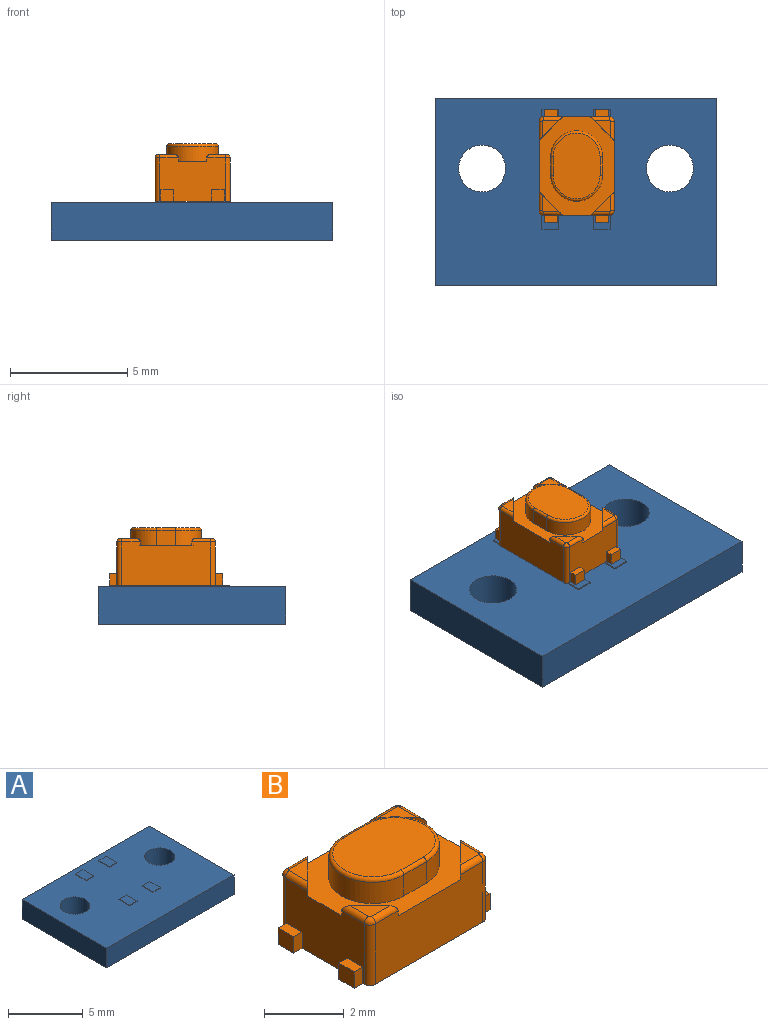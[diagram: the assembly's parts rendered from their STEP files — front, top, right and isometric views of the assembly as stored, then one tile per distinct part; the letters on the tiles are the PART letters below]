
ASSEMBLY  parts=2 mates=1
PART A: 28 faces, bbox 12x8x1.7 mm
  f0: plane 12x8mm, normal (0,0,1), area 86.9mm2, adj f1,f2,f3,f4,f5,f6,f8,f9
  f1: plane 12x1.6mm, normal (0,1,0), area 19.2mm2, adj f0,f2,f6,f7
  f2: plane 8x1.6mm, normal (-1,0,0), area 12.8mm2, adj f0,f1,f3,f7
  f3: plane 12x1.6mm, normal (0,-1,0), area 19.2mm2, adj f0,f2,f6,f7
  f4: cylinder r=1mm len=2mm, axis (0,0,-1), area 10.1mm2, adj f0,f7
  f5: cylinder r=1mm len=2mm, axis (0,0,-1), area 10.1mm2, adj f0,f7
  f6: plane 8x1.6mm, normal (1,0,0), area 12.8mm2, adj f0,f1,f3,f7
  f7: plane 12x8mm, normal (0,0,-1), area 89.7mm2, adj f1,f2,f3,f4,f5,f6
  f8: plane 1x0.05mm, normal (-1,0,0), area 0mm2, adj f0,f9,f11,f12
  f9: plane 0.7x0.05mm, normal (0,-1,0), area 0mm2, adj f0,f8,f10,f12
  f10: plane 1x0.05mm, normal (1,0,0), area 0mm2, adj f0,f9,f11,f12
  f11: plane 0.7x0.05mm, normal (0,1,0), area 0mm2, adj f0,f8,f10,f12
  f12: plane 1x0.7mm, normal (0,0,1), area 0.7mm2, adj f8,f9,f10,f11
  f13: plane 1x0.05mm, normal (-1,0,0), area 0mm2, adj f0,f14,f16,f17
  f14: plane 0.7x0.05mm, normal (0,-1,0), area 0mm2, adj f0,f13,f15,f17
  f15: plane 1x0.05mm, normal (1,0,0), area 0mm2, adj f0,f14,f16,f17
  f16: plane 0.7x0.05mm, normal (0,1,0), area 0mm2, adj f0,f13,f15,f17
  f17: plane 1x0.7mm, normal (0,0,1), area 0.7mm2, adj f13,f14,f15,f16
  f18: plane 1x0.05mm, normal (-1,0,0), area 0mm2, adj f0,f19,f21,f22
  f19: plane 0.7x0.05mm, normal (0,-1,0), area 0mm2, adj f0,f18,f20,f22
  f20: plane 1x0.05mm, normal (1,0,0), area 0mm2, adj f0,f19,f21,f22
  f21: plane 0.7x0.05mm, normal (0,1,0), area 0mm2, adj f0,f18,f20,f22
  f22: plane 1x0.7mm, normal (0,0,1), area 0.7mm2, adj f18,f19,f20,f21
  f23: plane 1x0.05mm, normal (-1,0,0), area 0mm2, adj f0,f24,f26,f27
  f24: plane 0.7x0.05mm, normal (0,-1,0), area 0mm2, adj f0,f23,f25,f27
  f25: plane 1x0.05mm, normal (1,0,0), area 0mm2, adj f0,f24,f26,f27
  f26: plane 0.7x0.05mm, normal (0,1,0), area 0mm2, adj f0,f23,f25,f27
  f27: plane 1x0.7mm, normal (0,0,1), area 0.7mm2, adj f23,f24,f25,f26
PART B: 55 faces, bbox 4.8x3.2x2.5 mm
  f0: plane 4.2x3.2mm, normal (0,0,1), area 5.9mm2, adj f1,f2,f3,f4,f26,f27,f28,f29
  f1: plane 3.8x1.85mm, normal (0,1,0), area 6.7mm2, adj f0,f5,f6,f9,f33,f35,f39,f50
  f2: plane 2.8x1.85mm, normal (-1,0,0), area 4.4mm2, adj f0,f5,f6,f7,f14,f15,f16,f22
  f3: plane 3.8x1.85mm, normal (0,-1,0), area 6.7mm2, adj f0,f5,f7,f8,f31,f37,f42,f47
  f4: plane 2.8x1.85mm, normal (1,0,0), area 4.4mm2, adj f0,f5,f8,f9,f11,f12,f13,f19
  f5: plane 4.8x3.2mm, normal (0,0,-1), area 14.1mm2, adj f1,f2,f3,f4,f6,f7,f8,f9
  f6: cylinder r=0.2mm len=1.85mm, axis (0,0,1), area 0.6mm2, adj f1,f2,f5,f49
  f7: cylinder r=0.2mm len=1.85mm, axis (0,0,-1), area 0.6mm2, adj f2,f3,f5,f46
  f8: cylinder r=0.2mm len=1.85mm, axis (0,0,1), area 0.6mm2, adj f3,f4,f5,f43
  f9: cylinder r=0.2mm len=1.85mm, axis (0,0,-1), area 0.6mm2, adj f1,f4,f5,f40
  f10: plane 0.55x0.5mm, normal (1,0,0), area 0.3mm2, adj f5,f11,f12,f13
  f11: plane 0.55x0.3mm, normal (0,0,1), area 0.2mm2, adj f4,f10,f12,f13
  f12: plane 0.5x0.3mm, normal (0,-1,0), area 0.2mm2, adj f4,f5,f10,f11
  f13: plane 0.5x0.3mm, normal (0,1,0), area 0.2mm2, adj f4,f5,f10,f11
  f14: plane 0.5x0.3mm, normal (0,1,0), area 0.2mm2, adj f2,f5,f16,f17
  f15: plane 0.5x0.3mm, normal (0,-1,0), area 0.2mm2, adj f2,f5,f16,f17
  f16: plane 0.55x0.3mm, normal (0,0,1), area 0.2mm2, adj f2,f14,f15,f17
  f17: plane 0.55x0.5mm, normal (-1,0,0), area 0.3mm2, adj f5,f14,f15,f16
  f18: plane 0.55x0.5mm, normal (1,0,0), area 0.3mm2, adj f5,f19,f20,f21
  f19: plane 0.55x0.3mm, normal (0,0,1), area 0.2mm2, adj f4,f18,f20,f21
  f20: plane 0.5x0.3mm, normal (0,-1,0), area 0.2mm2, adj f4,f5,f18,f19
  f21: plane 0.5x0.3mm, normal (0,1,0), area 0.2mm2, adj f4,f5,f18,f19
  f22: plane 0.55x0.3mm, normal (0,0,1), area 0.2mm2, adj f2,f23,f24,f25
  f23: plane 0.5x0.3mm, normal (0,1,0), area 0.2mm2, adj f2,f5,f22,f25
  f24: plane 0.5x0.3mm, normal (0,-1,0), area 0.2mm2, adj f2,f5,f22,f25
  f25: plane 0.55x0.5mm, normal (-1,0,0), area 0.3mm2, adj f5,f22,f23,f24
  f26: plane 0.8x0.65mm, normal (0,1,0), area 0.5mm2, adj f0,f27,f29,f51
  f27: cylinder r=1.1mm len=2.2mm, axis (0,0,-1), area 2.2mm2, adj f0,f26,f28,f53
  f28: plane 0.8x0.65mm, normal (0,-1,0), area 0.5mm2, adj f0,f27,f29,f54
  f29: cylinder r=1.1mm len=2.2mm, axis (0,0,-1), area 2.2mm2, adj f0,f26,f28,f52
  f30: plane 2.8x2mm, normal (0,0,1), area 4.7mm2, adj f51,f52,f53,f54
  f31: plane 1x1mm, normal (0.71,0.71,0), area 0.4mm2, adj f0,f2,f3,f32,f45,f47
  f32: plane 0.7x0.7mm, normal (0,0,1), area 0.2mm2, adj f31,f45,f46,f47
  f33: plane 1x1mm, normal (0.71,-0.71,0), area 0.4mm2, adj f0,f1,f2,f34,f48,f50
  f34: plane 0.7x0.7mm, normal (0,0,1), area 0.2mm2, adj f33,f48,f49,f50
  f35: plane 1x1mm, normal (-0.71,-0.71,0), area 0.4mm2, adj f0,f1,f4,f36,f39,f41
  f36: plane 0.7x0.7mm, normal (0,0,1), area 0.2mm2, adj f35,f39,f40,f41
  f37: plane 1x1mm, normal (-0.71,0.71,0), area 0.4mm2, adj f0,f3,f4,f38,f42,f44
  f38: plane 0.7x0.7mm, normal (0,0,1), area 0.2mm2, adj f37,f42,f43,f44
  f39: cylinder r=0.15mm len=0.8mm, axis (1,0,0), area 0.2mm2, adj f1,f35,f36,f40
  f40: torus R=0.05mm, axis (0,0,1), area 0.1mm2, adj f9,f36,f39,f41
  f41: cylinder r=0.15mm len=0.8mm, axis (0,-1,0), area 0.2mm2, adj f4,f35,f36,f40
  f42: cylinder r=0.15mm len=0.8mm, axis (-1,0,0), area 0.2mm2, adj f3,f37,f38,f43
  f43: torus R=0.05mm, axis (0,0,1), area 0.1mm2, adj f8,f38,f42,f44
  f44: cylinder r=0.15mm len=0.8mm, axis (0,-1,0), area 0.2mm2, adj f4,f37,f38,f43
  f45: cylinder r=0.15mm len=0.8mm, axis (0,1,0), area 0.2mm2, adj f2,f31,f32,f46
  f46: torus R=0.05mm, axis (0,0,1), area 0.1mm2, adj f7,f32,f45,f47
  f47: cylinder r=0.15mm len=0.8mm, axis (-1,0,0), area 0.2mm2, adj f3,f31,f32,f46
  f48: cylinder r=0.15mm len=0.8mm, axis (0,1,0), area 0.2mm2, adj f2,f33,f34,f49
  f49: torus R=0.05mm, axis (0,0,1), area 0.1mm2, adj f6,f34,f48,f50
  f50: cylinder r=0.15mm len=0.8mm, axis (1,0,0), area 0.2mm2, adj f1,f33,f34,f49
  f51: cylinder r=0.1mm len=0.8mm, axis (1,0,0), area 0.1mm2, adj f26,f30,f52,f53
  f52: torus R=1mm, axis (0,0,1), area 0.5mm2, adj f29,f30,f51,f54
  f53: torus R=1mm, axis (0,0,1), area 0.5mm2, adj f27,f30,f51,f54
  f54: cylinder r=0.1mm len=0.8mm, axis (-1,0,0), area 0.1mm2, adj f28,f30,f52,f53
PLACE A t=(13.25,-13.12,5.36)mm
PLACE B rot(axis=(0,0,-1),90deg) t=(-21.54,-30.25,7.01)mm
MATE fastened B.f5 <-> A.f27  axis (0,0,-1) through (-6.43,-7.12,7.01)mm
